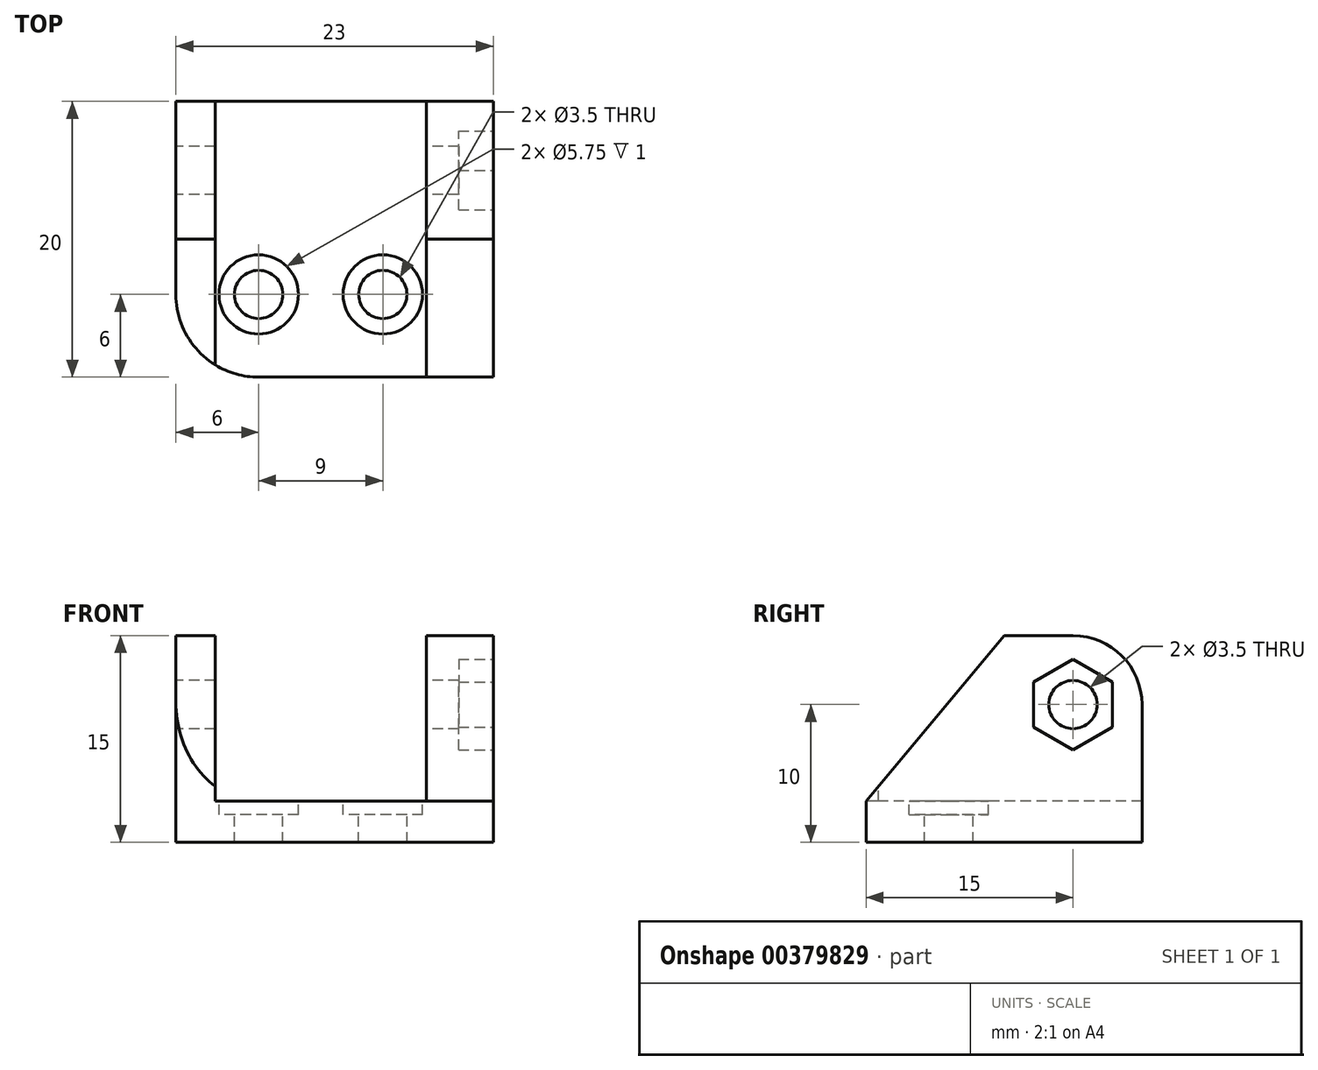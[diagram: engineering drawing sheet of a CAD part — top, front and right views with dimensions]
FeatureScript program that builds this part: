
annotation { "Feature Type Name" : "Feature", "Feature Type Description" : "" }
export const myFeature = defineFeature(function(context is Context, id is Id, definition is map)
    precondition{}
    {
        {
            var Q0;
            Q0=qCreatedBy(makeId("Top.planeOp"),FACE);
            var sketch = newSketch(context, id + "F0", { "sketchPlane" : qUnion([Q0])});
            skLineSegment(sketch, "E0.bottom", {"start": v(0, 0) * mm, "end": v(21, 0) * mm});
            skLineSegment(sketch, "E0.top", {"start": v(0, 20) * mm, "end": v(21, 20) * mm});
            skLineSegment(sketch, "E0.left", {"start": v(0, 0) * mm, "end": v(0, 20) * mm});
            skLineSegment(sketch, "E0.right", {"start": v(21, 0) * mm, "end": v(21, 20) * mm});
            skSolve(sketch);
        }
        {
            var Q0;
            Q0=qSketchRegion(id+"F0",true);
            extrude(context, id + "F1", {"entities" : qUnion([Q0]), "depth" : 3 * mm});
        }
        {
            var Q0;
            Q0=makeQuery(id+"F1.opExtrude","CAP_FACE",FACE,{"disambiguationData":[OSD([sQuery(id+"F0.wireOp",EDGE,"E0.bottom"),sQuery(id+"F0.wireOp",EDGE,"E0.top"),sQuery(id+"F0.wireOp",EDGE,"E0.left"),sQuery(id+"F0.wireOp",EDGE,"E0.right")])],"isStart":false});
            var sketch = newSketch(context, id + "F2", { "sketchPlane" : qUnion([Q0])});
            skLineSegment(sketch, "E1.bottom", {"start": v(0, 20) * mm, "end": v(2.85, 20) * mm});
            skLineSegment(sketch, "E1.top", {"start": v(0, 0) * mm, "end": v(2.85, 0) * mm});
            skLineSegment(sketch, "E1.left", {"start": v(0, 20) * mm, "end": v(0, 0) * mm});
            skLineSegment(sketch, "E1.right", {"start": v(2.85, 20) * mm, "end": v(2.85, 0) * mm});
            skLineSegment(sketch, "E2.bottom", {"start": v(21, 20) * mm, "end": v(18.15, 20) * mm});
            skLineSegment(sketch, "E2.top", {"start": v(21, 0) * mm, "end": v(18.15, 0) * mm});
            skLineSegment(sketch, "E2.left", {"start": v(21, 20) * mm, "end": v(21, 0) * mm});
            skLineSegment(sketch, "E2.right", {"start": v(18.15, 20) * mm, "end": v(18.15, 0) * mm});
            skSolve(sketch);
        }
        {
            var Q0;
            Q0=qSketchRegion(id+"F2",true);
            extrude(context, id + "F3", {"entities" : qUnion([Q0]), "operationType" : NewBodyOperationType.ADD, "depth" : 12 * mm});
        }
        {
            var Q0;
            Q0=makeQuery(id+"F3.boolean.opBoolean","MERGE",EDGE,{"derivedFrom":[makeQuery(id+"F1.opExtrude","SWEPT_EDGE",EDGE,{"disambiguationData":[OSD([sQuery(id+"F0.wireOp",EDGE,"E0.bottom"),sQuery(id+"F0.wireOp",EDGE,"E0.left")])]}),makeQuery(id+"F3.opExtrude","SWEPT_EDGE",EDGE,{"disambiguationData":[OSD([sQuery(id+"F2.wireOp",EDGE,"E1.top"),sQuery(id+"F2.wireOp",EDGE,"E1.left")])]})]});
            fillet(context, id + "F4", {"entities" : qUnion([Q0]), "radius" : 6 * mm, "tangentPropagation" : true, "allowEdgeOverflow" : false});
        }
        {
            var Q0;
            Q0=makeQuery(id+"F3.boolean.opBoolean","MERGE",FACE,{"derivedFrom":[makeQuery(id+"F1.opExtrude","SWEPT_FACE",FACE,{"disambiguationData":[OSD([sQuery(id+"F0.wireOp",EDGE,"E0.left")])]}),makeQuery(id+"F3.opExtrude","SWEPT_FACE",FACE,{"disambiguationData":[OSD([sQuery(id+"F2.wireOp",EDGE,"E1.left")])]})]});
            var sketch = newSketch(context, id + "F5", { "sketchPlane" : qUnion([Q0])});
            skCircle(sketch, "E3", {"center": v(-15, 10) * mm, "radius": 1.75 * mm});
            skLineSegment(sketch, "E4.0.1", {"start": v(0, 0) * mm, "end": v(0, 15) * mm, "construction": true});
            skLineSegment(sketch, "E4.0.3", {"start": v(0, 15) * mm, "end": v(0, 3) * mm, "construction": true});
            skLineSegment(sketch, "E5", {"start": v(-10, 15) * mm, "end": v(0, 3) * mm});
            skLineSegment(sketch, "E6", {"start": v(0, 16.5) * mm, "end": v(0, 3) * mm});
            skLineSegment(sketch, "E7.0.0", {"start": v(-20, 3) * mm, "end": v(0, 3) * mm, "construction": true});
            skLineSegment(sketch, "E7.0.1", {"start": v(0, 3) * mm, "end": v(0, 15) * mm, "construction": true});
            skLineSegment(sketch, "E7.0.2", {"start": v(0, 15) * mm, "end": v(-20, 15) * mm, "construction": true});
            skLineSegment(sketch, "E7.0.3", {"start": v(-20, 15) * mm, "end": v(-20, 3) * mm, "construction": true});
            skLineSegment(sketch, "E8", {"start": v(-10, 15) * mm, "end": v(0, 15) * mm});
            skLineSegment(sketch, "E9", {"start": v(0, 15) * mm, "end": v(0, 3) * mm});
            skSolve(sketch);
        }
        {
            var Q0;
            Q0=qSketchRegion(id+"F5",true);
            extrude(context, id + "F6", {"entities" : qUnion([Q0]), "operationType" : NewBodyOperationType.REMOVE, "endBound" : BoundingType.THROUGH_ALL, "oppositeDirection" : true, "depth" : 25 * mm});
        }
        {
            var Q0;
            Q0=makeQuery(id+"F3.opExtrude","CAP_EDGE",EDGE,{"disambiguationData":[OSD([sQuery(id+"F2.wireOp",EDGE,"E1.bottom")])],"isStart":false});
            var Q1;
            Q1=makeQuery(id+"F3.opExtrude","CAP_EDGE",EDGE,{"disambiguationData":[OSD([sQuery(id+"F2.wireOp",EDGE,"E2.bottom")])],"isStart":false});
            var Q2;
            {var subQ0=sQuery(id+"F2.wireOp",EDGE,"E1.left");var subQ1=sQuery(id+"F5.wireOp",EDGE,"E5");Q2=makeQuery(id+"F6.boolean.opBoolean","COPY",EDGE,{"disambiguationData":[topologyDisambiguationEdgeConnected([makeQuery(id+"F3.opExtrude","CAP_FACE",FACE,{"disambiguationData":[OSD([sQuery(id+"F2.wireOp",EDGE,"E1.bottom"),sQuery(id+"F2.wireOp",EDGE,"E1.top"),subQ0,sQuery(id+"F2.wireOp",EDGE,"E1.right")])],"isStart":false})])],"derivedFrom":makeQuery(id+"F6.opExtrude","SWEPT_EDGE",EDGE,{"disambiguationData":[OSD([subQ0,sQuery(id+"F5.wireOp",EDGE,"toCVR1km-wCAx-B5Tf-Qxij-KXW5aZ6ogp7M"),subQ1])]})});}
            var Q3;
            {var subQ0=sQuery(id+"F5.wireOp",EDGE,"E5");Q3=makeQuery(id+"F6.boolean.opBoolean","COPY",EDGE,{"disambiguationData":[topologyDisambiguationEdgeConnected([makeQuery(id+"F3.opExtrude","CAP_FACE",FACE,{"disambiguationData":[OSD([sQuery(id+"F2.wireOp",EDGE,"E2.bottom"),sQuery(id+"F2.wireOp",EDGE,"E2.top"),sQuery(id+"F2.wireOp",EDGE,"E2.left"),sQuery(id+"F2.wireOp",EDGE,"E2.right")])],"isStart":false})])],"derivedFrom":makeQuery(id+"F6.opExtrude","SWEPT_EDGE",EDGE,{"disambiguationData":[OSD([sQuery(id+"F2.wireOp",EDGE,"E1.left"),sQuery(id+"F5.wireOp",EDGE,"toCVR1km-wCAx-B5Tf-Qxij-KXW5aZ6ogp7M"),subQ0])]})});}
            var Q4;
            {var subQ0=sQuery(id+"F2.wireOp",EDGE,"E1.top");var subQ1=sQuery(id+"F0.wireOp",EDGE,"E0.left");var subQ2=sQuery(id+"F0.wireOp",EDGE,"E0.bottom");var subQ3=sQuery(id+"F2.wireOp",EDGE,"E1.left");var subQ4=sQuery(id+"F5.wireOp",EDGE,"E5");Q4=makeQuery(id+"F6.boolean.opBoolean","COPY",EDGE,{"disambiguationData":[TD([makeQuery(id+"F1.opExtrude","SWEPT_FACE",FACE,{"disambiguationData":[OSD([subQ1])]})])],"derivedFrom":makeQuery(id+"F6.opExtrude","SWEPT_EDGE",EDGE,{"disambiguationData":[OSD([subQ2,subQ1,subQ0,subQ3,subQ4,sQuery(id+"F5.wireOp",EDGE,"E6")])]})});}
            fillet(context, id + "F7", {"entities" : qUnion([Q0, Q1, Q2, Q3, Q4]), "radius" : 5 * mm, "tangentPropagation" : true, "allowEdgeOverflow" : false});
        }
        {
            var Q0;
            Q0=makeQuery(id+"F1.opExtrude","CAP_FACE",FACE,{"disambiguationData":[OSD([sQuery(id+"F0.wireOp",EDGE,"E0.bottom"),sQuery(id+"F0.wireOp",EDGE,"E0.top"),sQuery(id+"F0.wireOp",EDGE,"E0.left"),sQuery(id+"F0.wireOp",EDGE,"E0.right")])],"isStart":false});
            var sketch = newSketch(context, id + "F8", { "sketchPlane" : qUnion([Q0])});
            skCircle(sketch, "E10", {"center": v(6, 6) * mm, "radius": 1.75 * mm});
            skCircle(sketch, "E11", {"center": v(15, 6) * mm, "radius": 1.75 * mm});
            skSolve(sketch);
        }
        {
            var Q0;
            Q0=qSketchRegion(id+"F8",true);
            extrude(context, id + "F9", {"entities" : qUnion([Q0]), "operationType" : NewBodyOperationType.REMOVE, "endBound" : BoundingType.THROUGH_ALL, "oppositeDirection" : true, "depth" : 25 * mm});
        }
        {
            var Q0;
            Q0=makeQuery(id+"F3.boolean.opBoolean","MERGE",FACE,{"derivedFrom":[makeQuery(id+"F1.opExtrude","SWEPT_FACE",FACE,{"disambiguationData":[OSD([sQuery(id+"F0.wireOp",EDGE,"E0.right")])]}),makeQuery(id+"F3.opExtrude","SWEPT_FACE",FACE,{"disambiguationData":[OSD([sQuery(id+"F2.wireOp",EDGE,"E2.left")])]})]});
            extrude(context, id + "F10", {"entities" : qUnion([Q0]), "operationType" : NewBodyOperationType.ADD, "depth" : 2 * mm});
        }
        {
            var Q0;
            Q0=makeQuery(id+"F10.opExtrude","CAP_FACE",FACE,{"disambiguationData":[OSD([sQuery(id+"F0.wireOp",EDGE,"E0.right"),sQuery(id+"F2.wireOp",EDGE,"E2.left")])],"isStart":false});
            var sketch = newSketch(context, id + "F11", { "sketchPlane" : qUnion([Q0])});
            skCircle(sketch, "E12.cCircle", {"center": v(15, 10) * mm, "radius": 2.85 * mm, "construction": true});
            skLineSegment(sketch, "E12.0", {"start": v(17.85, 11.65) * mm, "end": v(17.85, 8.35) * mm});
            skLineSegment(sketch, "E12.1", {"start": v(17.85, 8.35) * mm, "end": v(15, 6.7) * mm});
            skLineSegment(sketch, "E12.2", {"start": v(15, 6.7) * mm, "end": v(12.15, 8.35) * mm});
            skLineSegment(sketch, "E12.3", {"start": v(12.15, 8.35) * mm, "end": v(12.15, 11.65) * mm});
            skLineSegment(sketch, "E12.4", {"start": v(12.15, 11.65) * mm, "end": v(15, 13.3) * mm});
            skLineSegment(sketch, "E12.5", {"start": v(15, 13.3) * mm, "end": v(17.85, 11.65) * mm});
            skPoint(sketch, "E12.0.midPoint", {"position": v(17.85, 10) * mm});
            skSolve(sketch);
        }
        {
            var Q0;
            Q0=qSketchRegion(id+"F11",true);
            extrude(context, id + "F12", {"entities" : qUnion([Q0]), "operationType" : NewBodyOperationType.REMOVE, "oppositeDirection" : true, "depth" : 2.5 * mm});
        }
        {
            var Q0;
            Q0=makeQuery(id+"F1.opExtrude","CAP_FACE",FACE,{"disambiguationData":[OSD([sQuery(id+"F0.wireOp",EDGE,"E0.bottom"),sQuery(id+"F0.wireOp",EDGE,"E0.top"),sQuery(id+"F0.wireOp",EDGE,"E0.left"),sQuery(id+"F0.wireOp",EDGE,"E0.right")])],"isStart":false});
            var sketch = newSketch(context, id + "F13", { "sketchPlane" : qUnion([Q0])});
            skCircle(sketch, "E13.0", {"center": v(6, 6) * mm, "radius": 1.75 * mm, "construction": true});
            skCircle(sketch, "E14.0", {"center": v(15, 6) * mm, "radius": 1.75 * mm, "construction": true});
            skCircle(sketch, "E15", {"center": v(6, 6) * mm, "radius": 2.88 * mm});
            skCircle(sketch, "E16", {"center": v(15, 6) * mm, "radius": 2.88 * mm});
            skSolve(sketch);
        }
        {
            var Q0;
            Q0 = qSketchRegion(id + "F13", true);
            extrude(context, id + "F14", {"entities" : qUnion([Q0]), "operationType" : NewBodyOperationType.REMOVE, "oppositeDirection" : true, "depth" : 1 * mm});
        }
    });
